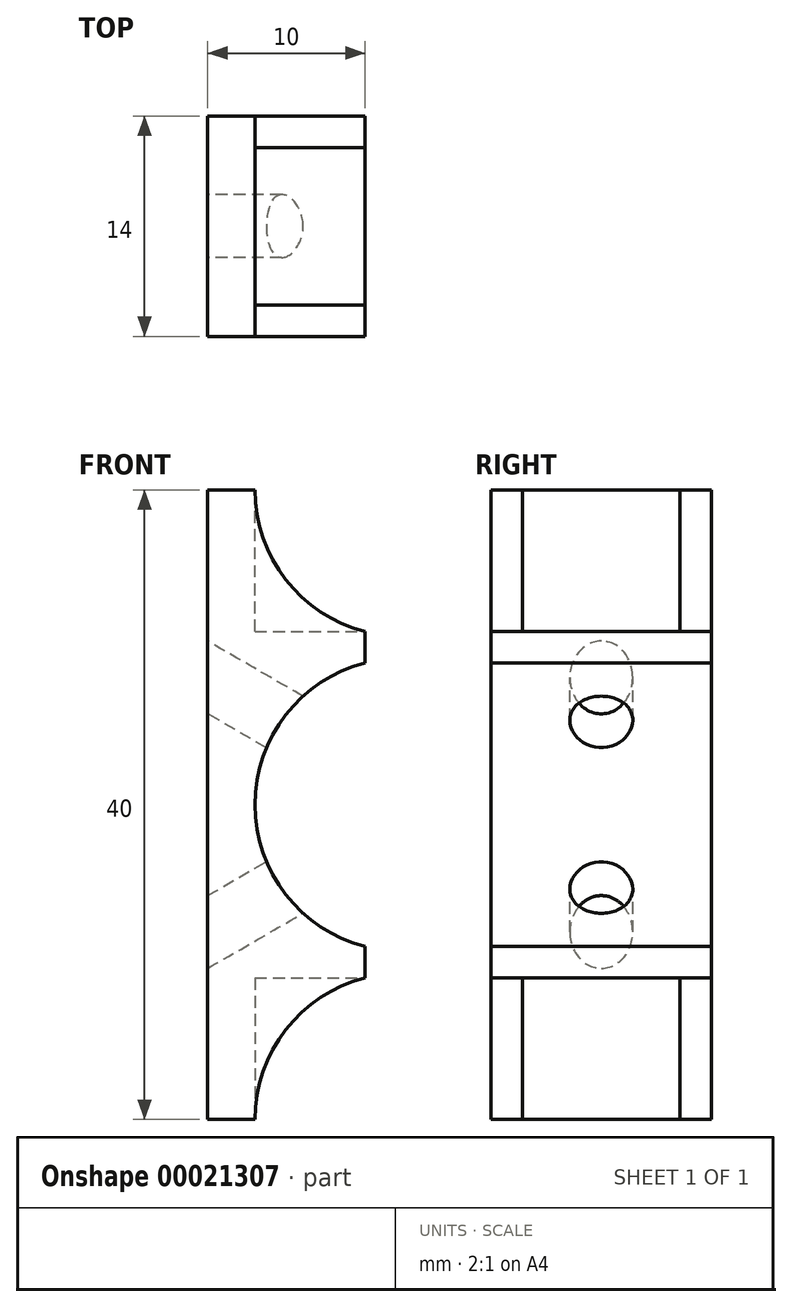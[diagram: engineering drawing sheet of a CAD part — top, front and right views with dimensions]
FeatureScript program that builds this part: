
annotation { "Feature Type Name" : "Feature", "Feature Type Description" : "" }
export const myFeature = defineFeature(function(context is Context, id is Id, definition is map)
    precondition{}
    {
        {
            var Q0;
            Q0=qCreatedBy(makeId("Front.planeOp"),FACE);
            var sketch = newSketch(context, id + "F0", { "sketchPlane" : qUnion([Q0])});
            skLineSegment(sketch, "E0.bottom", {"start": v(-20, 3) * mm, "end": v(20, 3) * mm, "construction": true});
            skLineSegment(sketch, "E0.top", {"start": v(-20, 0) * mm, "end": v(20, 0) * mm});
            skLineSegment(sketch, "E0.left", {"start": v(-20, 3) * mm, "end": v(-20, 0) * mm});
            skLineSegment(sketch, "E0.right", {"start": v(20, 3) * mm, "end": v(20, 0) * mm});
            skArc(sketch, "E1", {"start": v(-9, 10) * mm, "mid": v(0, 3) * mm, "end": v(9, 10) * mm});
            skArc(sketch, "E2", {"start": v(-20, 3) * mm, "mid": v(-14.3, 4.96) * mm, "end": v(-11, 10) * mm});
            skLineSegment(sketch, "E3", {"start": v(-11, 10) * mm, "end": v(-9, 10) * mm});
            skLineSegment(sketch, "E4.MirrorCS", {"start": v(11, 10) * mm, "end": v(9, 10) * mm});
            skArc(sketch, "E5.MirrorCS", {"start": v(20, 3) * mm, "mid": v(14.3, 4.96) * mm, "end": v(11, 10) * mm});
            skSolve(sketch);
        }
        {
            var Q0;
            Q0=makeQuery(id+"F0.imprint","IMPRINT",FACE,{"disambiguationData":[TD([[makeQuery(id+"F0.imprint","IMPRINT",EDGE,{"derivedFrom":sQuery(id+"F0.wireOp",EDGE,"E0.top")}),1.0]])]});
            extrude(context, id + "F1", {"entities" : qUnion([Q0]), "endBound" : BoundingType.SYMMETRIC, "depth" : 14 * mm});
        }
        {
            var Q0;
            Q0=makeQuery(id+"F1.opExtrude","SWEPT_FACE",FACE,{"disambiguationData":[OSD([sQuery(id+"F0.wireOp",EDGE,"E3")])]});
            var sketch = newSketch(context, id + "F2", { "sketchPlane" : qUnion([Q0])});
            skLineSegment(sketch, "E6.bottom", {"start": v(-11, 5) * mm, "end": v(-20, 5) * mm});
            skLineSegment(sketch, "E6.top", {"start": v(-11, -5) * mm, "end": v(-20, -5) * mm});
            skLineSegment(sketch, "E6.left", {"start": v(-11, 5) * mm, "end": v(-11, -5) * mm});
            skLineSegment(sketch, "E6.right", {"start": v(-20, 5) * mm, "end": v(-20, -5) * mm});
            skLineSegment(sketch, "E7.0", {"start": v(-20, -7) * mm, "end": v(-20, 7) * mm, "construction": true});
            skLineSegment(sketch, "E8.MirrorCS", {"start": v(11, 5) * mm, "end": v(20, 5) * mm});
            skLineSegment(sketch, "E9.MirrorCS", {"start": v(20, 5) * mm, "end": v(20, -5) * mm});
            skLineSegment(sketch, "E10.MirrorCS", {"start": v(11, 5) * mm, "end": v(11, -5) * mm});
            skLineSegment(sketch, "E11.MirrorCS", {"start": v(11, -5) * mm, "end": v(20, -5) * mm});
            skSolve(sketch);
        }
        {
            var Q0;
            Q0=makeQuery(id+"F2.imprint","IMPRINT",FACE,{"disambiguationData":[TD([[makeQuery(id+"F2.imprint","IMPRINT",EDGE,{"derivedFrom":sQuery(id+"F2.wireOp",EDGE,"E6.bottom")}),1.0]])]});
            var Q1;
            Q1=makeQuery(id+"F2.imprint","IMPRINT",FACE,{"disambiguationData":[TD([[makeQuery(id+"F2.imprint","IMPRINT",EDGE,{"derivedFrom":sQuery(id+"F2.wireOp",EDGE,"E8.MirrorCS")}),-1.0]])]});
            extrude(context, id + "F3", {"entities" : qUnion([Q0, Q1]), "operationType" : NewBodyOperationType.REMOVE, "oppositeDirection" : true, "depth" : 7 * mm});
        }
        {
            var Q0;
            Q0=makeQuery(id+"F1.opExtrude","SWEPT_FACE",FACE,{"disambiguationData":[OSD([sQuery(id+"F0.wireOp",EDGE,"E0.top")])]});
            var sketch = newSketch(context, id + "F4", { "sketchPlane" : qUnion([Q0])});
            skLineSegment(sketch, "E12", {"start": v(0, 7) * mm, "end": v(0, -7) * mm, "construction": true});
            skSolve(sketch);
        }
        {
            var Q0;
            Q0=sQuery(id+"F4.wireOp",EDGE,"E12");
            cPlane(context, id + "F5", {"entities" : qUnion([Q0]), "cplaneType" : CPlaneType.LINE_ANGLE, "offset" : 150 * mm, "angle" : 30 * degree, "width" : 150 * mm, "height" : 150 * mm});
        }
        {
            var Q0;
            Q0=qCreatedBy(id+"F5.planeOp",FACE);
            var sketch = newSketch(context, id + "F6", { "sketchPlane" : qUnion([Q0])});
            skCircle(sketch, "E13", {"center": v(-7, 0) * mm, "radius": 2 * mm});
            skSolve(sketch);
        }
        {
            var Q0;
            Q0=makeQuery(id+"F6.imprint","IMPRINT",FACE,{"disambiguationData":[TD([[makeQuery(id+"F6.imprint","IMPRINT",EDGE,{"derivedFrom":sQuery(id+"F6.wireOp",EDGE,"E13")}),1.0]])]});
            extrude(context, id + "F7", {"entities" : qUnion([Q0]), "operationType" : NewBodyOperationType.REMOVE, "endBound" : BoundingType.SYMMETRIC, "depth" : 20 * mm});
        }
        {
            var Q0;
            Q0 = qBodyType(qCreatedBy(id + "F4" ,EDGE), BodyType.WIRE);
            cPlane(context, id + "F8", {"entities" : qUnion([Q0]), "cplaneType" : CPlaneType.LINE_ANGLE, "offset" : 150 * mm, "angle" : 330 * degree, "width" : 150 * mm, "height" : 150 * mm});
        }
        {
            var Q0;
            Q0=qCreatedBy(id+"F8.planeOp",FACE);
            var sketch = newSketch(context, id + "F9", { "sketchPlane" : qUnion([Q0])});
            skCircle(sketch, "E14", {"center": v(7, 0) * mm, "radius": 2 * mm});
            skSolve(sketch);
        }
        {
            var Q0;
            Q0=makeQuery(id+"F9.imprint","IMPRINT",FACE,{"disambiguationData":[TD([[makeQuery(id+"F9.imprint","IMPRINT",EDGE,{"derivedFrom":sQuery(id+"F9.wireOp",EDGE,"E14")}),1.0]])]});
            extrude(context, id + "F10", {"entities" : qUnion([Q0]), "operationType" : NewBodyOperationType.REMOVE, "endBound" : BoundingType.SYMMETRIC, "oppositeDirection" : true, "depth" : 20 * mm});
        }
        {
            var Q0;
            Q0=makeQuery(id+"F1.opExtrude","SWEPT_BODY",BODY,{"disambiguationData":[OSD([sQuery(id+"F0.wireOp",EDGE,"E0.top"),sQuery(id+"F0.wireOp",EDGE,"E0.left"),sQuery(id+"F0.wireOp",EDGE,"E0.right"),sQuery(id+"F0.wireOp",EDGE,"E1"),sQuery(id+"F0.wireOp",EDGE,"E2"),sQuery(id+"F0.wireOp",EDGE,"E3"),sQuery(id+"F0.wireOp",EDGE,"E4.MirrorCS"),sQuery(id+"F0.wireOp",EDGE,"E5.MirrorCS")])]});
            var Q1;
            Q1=sQuery(id+"F4.wireOp",EDGE,"E12");
            transform(context, id + "F11", {"entities" : qUnion([Q0]), "transformType" : TransformType.ROTATION, "transformAxis" : qUnion([Q1]), "angle" : 90 * degree, "makeCopy" : false});
        }
    });
